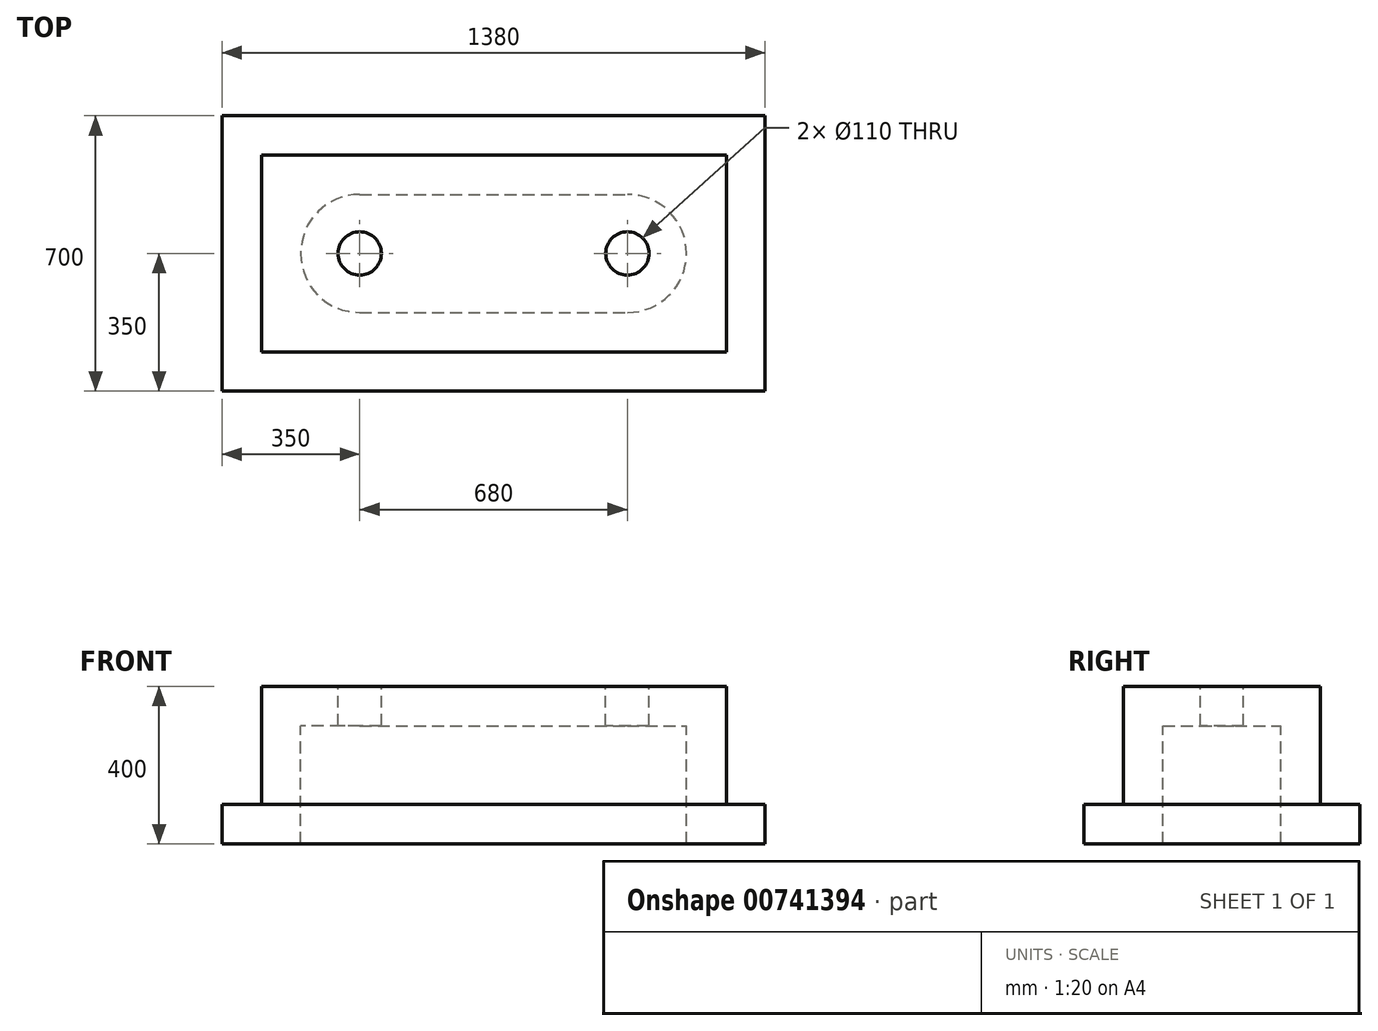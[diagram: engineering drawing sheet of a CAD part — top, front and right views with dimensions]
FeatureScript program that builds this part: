
annotation { "Feature Type Name" : "Feature", "Feature Type Description" : "" }
export const myFeature = defineFeature(function(context is Context, id is Id, definition is map)
    precondition{}
    {
        {
            var Q0;
            Q0=qCreatedBy(makeId("Top.planeOp"),FACE);
            var sketch = newSketch(context, id + "F0", { "sketchPlane" : qUnion([Q0])});
            skLineSegment(sketch, "E0.bottom", {"start": v(-590, -250) * mm, "end": v(590, -250) * mm});
            skLineSegment(sketch, "E0.top", {"start": v(-590, 250) * mm, "end": v(590, 250) * mm});
            skLineSegment(sketch, "E0.left", {"start": v(-590, -250) * mm, "end": v(-590, 250) * mm});
            skLineSegment(sketch, "E0.right", {"start": v(590, -250) * mm, "end": v(590, 250) * mm});
            skPoint(sketch, "E0.middle", {"position": v(0, 0) * mm});
            skLineSegment(sketch, "E1.bottom", {"start": v(-690, -350) * mm, "end": v(690, -350) * mm});
            skLineSegment(sketch, "E1.top", {"start": v(-690, 350) * mm, "end": v(690, 350) * mm});
            skLineSegment(sketch, "E1.left", {"start": v(-690, -350) * mm, "end": v(-690, 350) * mm});
            skLineSegment(sketch, "E1.right", {"start": v(690, -350) * mm, "end": v(690, 350) * mm});
            skSolve(sketch);
        }
        {
            var Q0;
            Q0 = qSketchRegion(id + "F0", true);
            var Q1;
            Q1=makeQuery(id+"F0.imprint","IMPRINT",FACE,{"disambiguationData":[TD([[makeQuery(id+"F0.imprint","IMPRINT",EDGE,{"derivedFrom":sQuery(id+"F0.wireOp",EDGE,"E0.bottom")}),1.0]])]});
            extrude(context, id + "F1", {"entities" : qUnion([Q0, Q1]), "depth" : 100 * mm, "offsetDistance" : 25 * mm});
        }
        {
            var Q0;
            Q0=makeQuery(id+"F1.opExtrude","CAP_FACE",FACE,{"disambiguationData":[OSD([sQuery(id+"F0.wireOp",EDGE,"E1.bottom"),sQuery(id+"F0.wireOp",EDGE,"E1.top"),sQuery(id+"F0.wireOp",EDGE,"E1.left"),sQuery(id+"F0.wireOp",EDGE,"E1.right")])],"isStart":false});
            var sketch = newSketch(context, id + "F2", { "sketchPlane" : qUnion([Q0])});
            skLineSegment(sketch, "E2.bottom", {"start": v(591.1, 250) * mm, "end": v(-588.9, 250) * mm});
            skLineSegment(sketch, "E2.top", {"start": v(591.1, -250) * mm, "end": v(-588.9, -250) * mm});
            skLineSegment(sketch, "E2.left", {"start": v(591.1, 250) * mm, "end": v(591.1, -250) * mm});
            skLineSegment(sketch, "E2.right", {"start": v(-588.9, 250) * mm, "end": v(-588.9, -250) * mm});
            skSolve(sketch);
        }
        {
            var Q0;
            Q0 = qSketchRegion(id + "F2", true);
            extrude(context, id + "F3", {"entities" : qUnion([Q0]), "operationType" : NewBodyOperationType.ADD, "depth" : 300 * mm, "offsetDistance" : 25 * mm});
        }
        {
            var Q0;
            Q0=makeQuery(id+"F3.opExtrude","CAP_FACE",FACE,{"disambiguationData":[OSD([sQuery(id+"F2.wireOp",EDGE,"E2.bottom"),sQuery(id+"F2.wireOp",EDGE,"E2.top"),sQuery(id+"F2.wireOp",EDGE,"E2.left"),sQuery(id+"F2.wireOp",EDGE,"E2.right")])],"isStart":false});
            var sketch = newSketch(context, id + "F4", { "sketchPlane" : qUnion([Q0])});
            skLineSegment(sketch, "E3.bottom", {"start": v(-340, -150) * mm, "end": v(340, -150) * mm});
            skLineSegment(sketch, "E3.top", {"start": v(-340, 150) * mm, "end": v(340, 150) * mm});
            skPoint(sketch, "E3.middle", {"position": v(0, 0) * mm});
            skArc(sketch, "E4", {"start": v(-340, 150) * mm, "mid": v(-490, 0) * mm, "end": v(-340, -150) * mm});
            skArc(sketch, "E5", {"start": v(340, -150) * mm, "mid": v(490, 0) * mm, "end": v(340, 150) * mm});
            skCircle(sketch, "E6", {"center": v(-340, 0) * mm, "radius": 55 * mm});
            skCircle(sketch, "E7", {"center": v(340, 0) * mm, "radius": 55 * mm});
            skSolve(sketch);
        }
        {
            var Q0;
            {var subQ0=sQuery(id+"F4.wireOp",EDGE,"E4");var subQ1=makeQuery(id+"F4.imprint","INTERSECT",VERTEX,{"derivedFrom":[sQuery(id+"F4.wireOp",EDGE,"E3.bottom"),subQ0]});Q0=makeQuery(id+"F4.imprint","IMPRINT",FACE,{"disambiguationData":[TD([[makeQuery(id+"F4.imprint","IMPRINT",EDGE,{"disambiguationData":[TD([[subQ1,1.0]])],"derivedFrom":subQ0}),1.0]])]});}
            var Q1;
            {var subQ0=sQuery(id+"F4.wireOp",EDGE,"E3.bottom");Q1=makeQuery(id+"F4.imprint","IMPRINT",FACE,{"disambiguationData":[TD([[makeQuery(id+"F4.imprint","IMPRINT",EDGE,{"derivedFrom":subQ0}),1.0]])]});}
            var Q2;
            {var subQ0=sQuery(id+"F4.wireOp",EDGE,"E5");var subQ1=makeQuery(id+"F4.imprint","INTERSECT",VERTEX,{"derivedFrom":[sQuery(id+"F4.wireOp",EDGE,"E3.bottom"),subQ0]});Q2=makeQuery(id+"F4.imprint","IMPRINT",FACE,{"disambiguationData":[TD([[makeQuery(id+"F4.imprint","IMPRINT",EDGE,{"disambiguationData":[TD([[subQ1,1.0]])],"derivedFrom":subQ0}),1.0]])]});}
            extrude(context, id + "F5", {"entities" : qUnion([Q0, Q1, Q2]), "operationType" : NewBodyOperationType.REMOVE, "endBound" : BoundingType.THROUGH_ALL, "depth" : 25 * mm, "offsetDistance" : 25 * mm});
        }
        {
            var Q0;
            Q0 = qSketchRegion(id + "F4", true);
            extrude(context, id + "F6", {"entities" : qUnion([Q0]), "operationType" : NewBodyOperationType.REMOVE, "endBound" : BoundingType.THROUGH_ALL, "oppositeDirection" : true, "depth" : 25 * mm, "offsetDistance" : 25 * mm});
        }
        {
            var Q0;
            Q0=makeQuery(id+"F6.boolean.opBoolean","SPLIT",FACE,{"disambiguationData":[TD([makeQuery(id+"F6.opExtrude","SWEPT_FACE",FACE,{"disambiguationData":[OSD([sQuery(id+"F4.wireOp",EDGE,"E6")])]})])],"derivedFrom":makeQuery(id+"F3.opExtrude","CAP_FACE",FACE,{"disambiguationData":[OSD([sQuery(id+"F2.wireOp",EDGE,"E2.bottom"),sQuery(id+"F2.wireOp",EDGE,"E2.top"),sQuery(id+"F2.wireOp",EDGE,"E2.left"),sQuery(id+"F2.wireOp",EDGE,"E2.right")])],"isStart":false})});
            var Q1;
            Q1=makeQuery(id+"F6.boolean.opBoolean","SPLIT",FACE,{"disambiguationData":[TD([makeQuery(id+"F6.opExtrude","SWEPT_FACE",FACE,{"disambiguationData":[OSD([sQuery(id+"F4.wireOp",EDGE,"E7")])]})])],"derivedFrom":makeQuery(id+"F3.opExtrude","CAP_FACE",FACE,{"disambiguationData":[OSD([sQuery(id+"F2.wireOp",EDGE,"E2.bottom"),sQuery(id+"F2.wireOp",EDGE,"E2.top"),sQuery(id+"F2.wireOp",EDGE,"E2.left"),sQuery(id+"F2.wireOp",EDGE,"E2.right")])],"isStart":false})});
            extrude(context, id + "F7", {"entities" : qUnion([Q0, Q1]), "operationType" : NewBodyOperationType.REMOVE, "endBound" : BoundingType.THROUGH_ALL, "oppositeDirection" : true, "depth" : 25 * mm, "offsetDistance" : 25 * mm});
        }
        {
            var Q0;
            Q0 = qSketchRegion(id + "F4", true);
            extrude(context, id + "F8", {"entities" : qUnion([Q0]), "operationType" : NewBodyOperationType.ADD, "oppositeDirection" : true, "depth" : 100 * mm, "offsetDistance" : 25 * mm});
        }
    });
